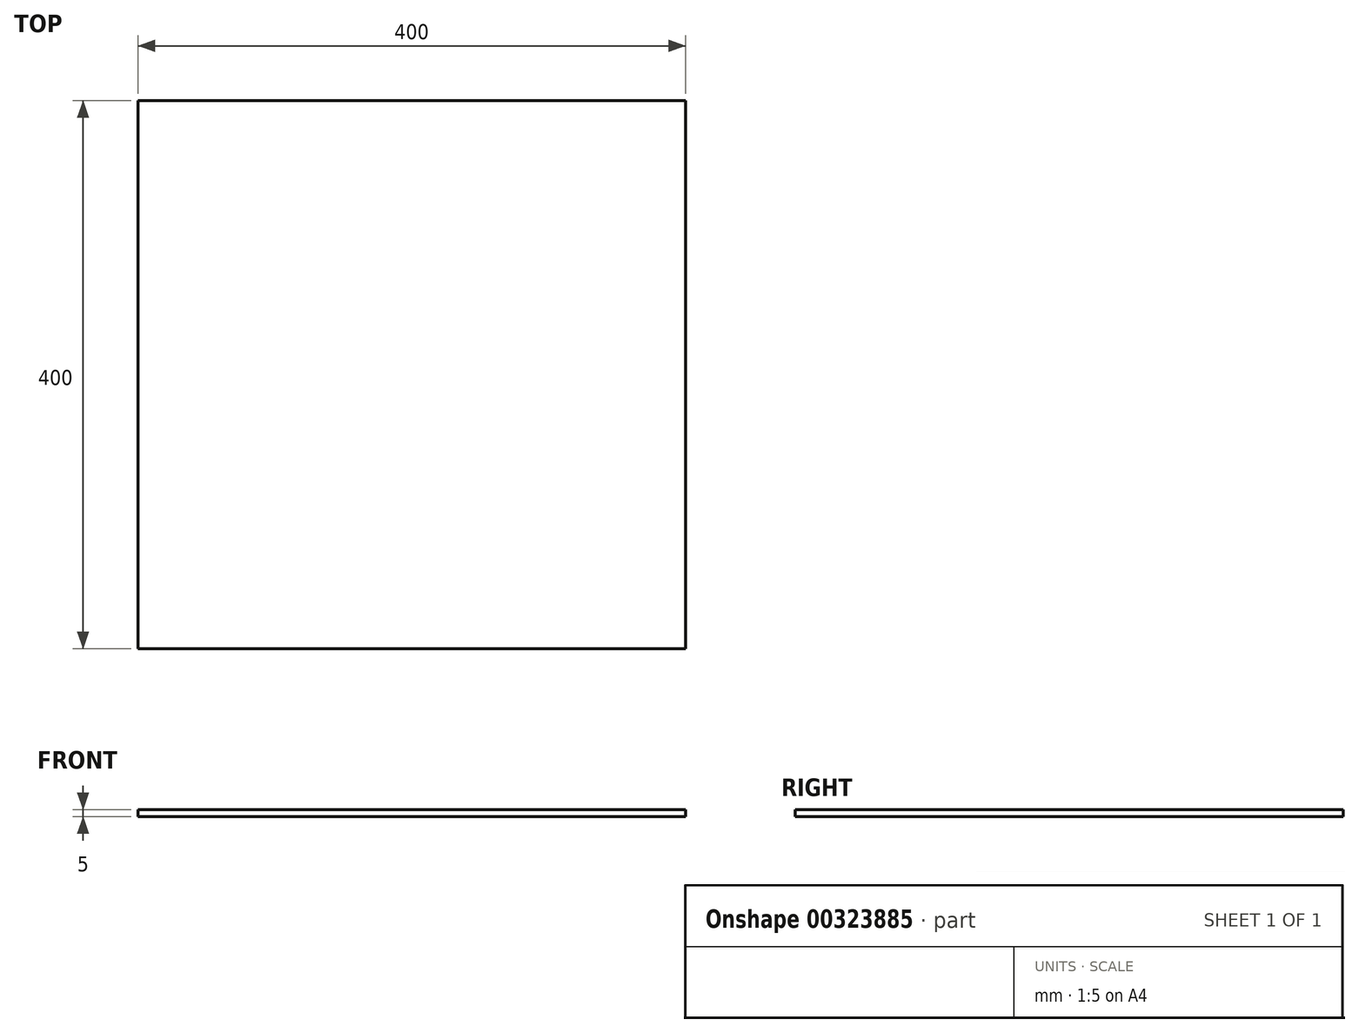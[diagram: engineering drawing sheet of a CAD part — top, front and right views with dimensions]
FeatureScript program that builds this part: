
annotation { "Feature Type Name" : "Feature", "Feature Type Description" : "" }
export const myFeature = defineFeature(function(context is Context, id is Id, definition is map)
    precondition{}
    {
        {
            var Q0;
            Q0=qCreatedBy(makeId("Top.planeOp"),FACE);
            var sketch = newSketch(context, id + "F0", { "sketchPlane" : qUnion([Q0])});
            skLineSegment(sketch, "E0.bottom", {"start": v(-200, 200) * mm, "end": v(200, 200) * mm});
            skLineSegment(sketch, "E0.top", {"start": v(-200, -200) * mm, "end": v(200, -200) * mm});
            skLineSegment(sketch, "E0.right", {"start": v(200, 200) * mm, "end": v(200, -200) * mm});
            skLineSegment(sketch, "E1", {"start": v(-200, 200) * mm, "end": v(-200, -200) * mm});
            skSolve(sketch);
        }
        {
            var Q0;
            {var subQ3=sQuery(id+"F0.wireOp",EDGE,"E0.bottom");Q0=makeQuery(id+"F0.imprint","IMPRINT",FACE,{"disambiguationData":[TD([[makeQuery(id+"F0.imprint","IMPRINT",EDGE,{"derivedFrom":subQ3}),-1.0]])]});}
            extrude(context, id + "F1", {"entities" : qUnion([Q0]), "depth" : 5 * mm});
        }
    });
